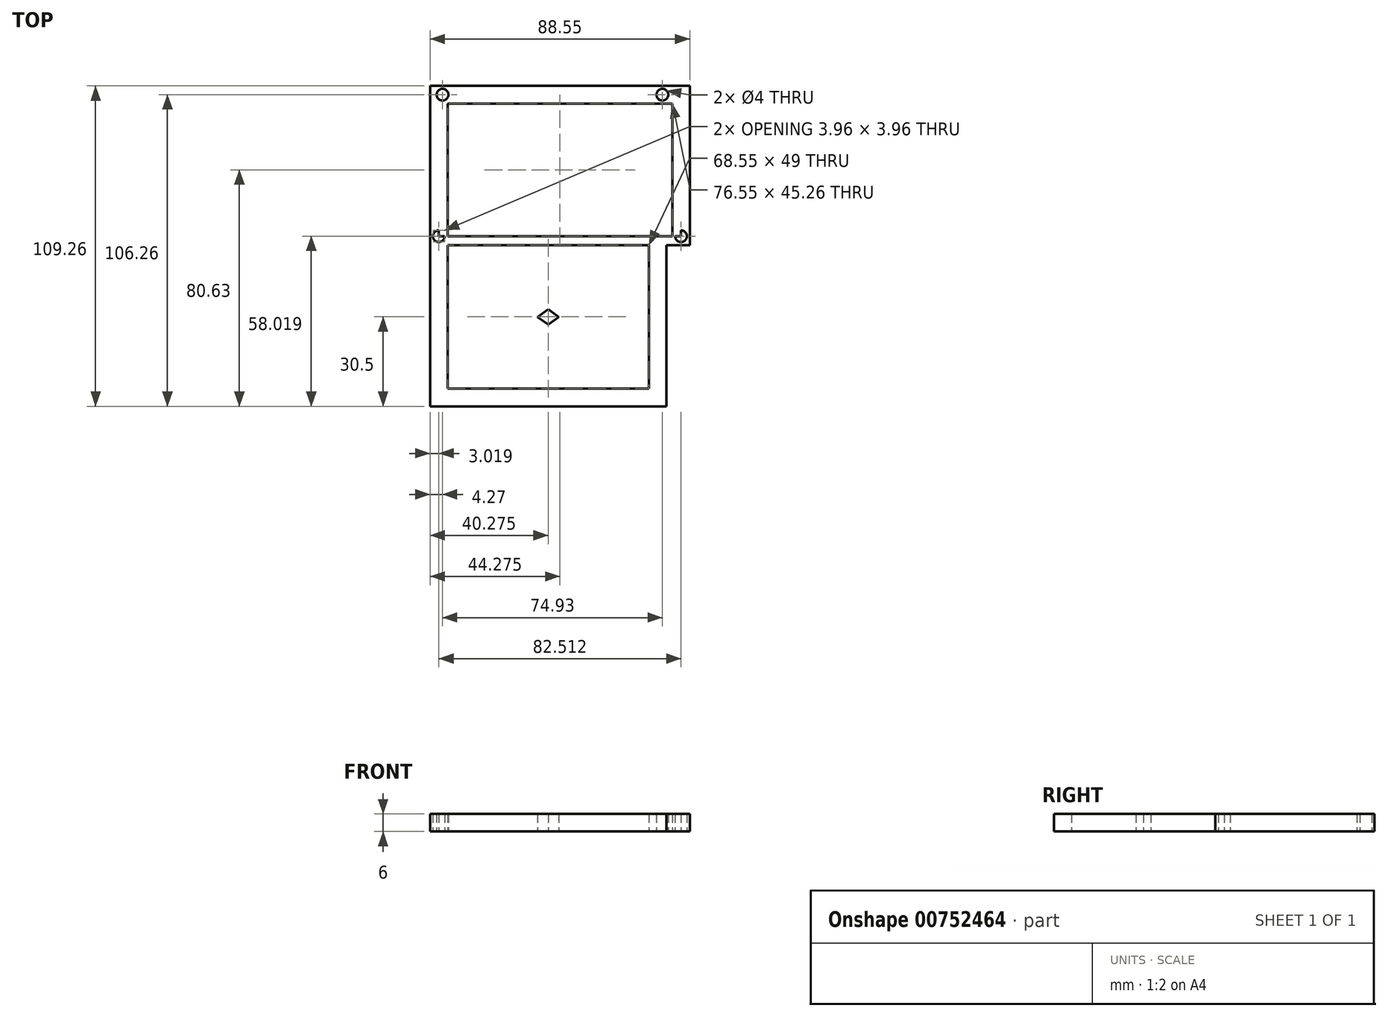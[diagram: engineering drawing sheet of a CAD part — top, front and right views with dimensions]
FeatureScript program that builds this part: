
annotation { "Feature Type Name" : "Feature", "Feature Type Description" : "" }
export const myFeature = defineFeature(function(context is Context, id is Id, definition is map)
    precondition{}
    {
        {
            var Q0;
            Q0=qCreatedBy(makeId("Top.planeOp"),FACE);
            var sketch = newSketch(context, id + "F0", { "sketchPlane" : qUnion([Q0])});
            skLineSegment(sketch, "E0", {"start": v(0, 0) * mm, "end": v(82.55, 0) * mm});
            skLineSegment(sketch, "E1", {"start": v(0, 0) * mm, "end": v(0, 48.26) * mm});
            skLineSegment(sketch, "E2", {"start": v(0, 48.26) * mm, "end": v(1.27, 48.26) * mm});
            skLineSegment(sketch, "E3", {"start": v(1.27, 48.26) * mm, "end": v(76.2, 48.26) * mm});
            skLineSegment(sketch, "E4", {"start": v(82.55, 0) * mm, "end": v(85.55, 0) * mm});
            skLineSegment(sketch, "E5", {"start": v(82.55, 0) * mm, "end": v(82.55, -3) * mm});
            skLineSegment(sketch, "E6", {"start": v(0, 0) * mm, "end": v(0, -3) * mm});
            skLineSegment(sketch, "E7", {"start": v(0, 0) * mm, "end": v(-3, 0) * mm});
            skLineSegment(sketch, "E8", {"start": v(0, 48.26) * mm, "end": v(-3, 48.26) * mm});
            skLineSegment(sketch, "E9", {"start": v(0, 48.26) * mm, "end": v(0, 51.26) * mm});
            skLineSegment(sketch, "E10", {"start": v(0, 51.26) * mm, "end": v(-3, 51.26) * mm});
            skLineSegment(sketch, "E11", {"start": v(-3, 51.26) * mm, "end": v(-3, 48.26) * mm});
            skLineSegment(sketch, "E12", {"start": v(0, -3) * mm, "end": v(-3, -3) * mm});
            skLineSegment(sketch, "E13", {"start": v(-3, 0) * mm, "end": v(-3, 48.26) * mm});
            skLineSegment(sketch, "E14", {"start": v(-3, 0) * mm, "end": v(-3, -3) * mm});
            skLineSegment(sketch, "E15", {"start": v(83.3, -3) * mm, "end": v(0, -3) * mm});
            skLineSegment(sketch, "E16", {"start": v(82.55, -3) * mm, "end": v(85.55, -3) * mm});
            skLineSegment(sketch, "E17", {"start": v(85.55, -3) * mm, "end": v(85.55, 0) * mm});
            skLineSegment(sketch, "E18", {"start": v(85.55, 0) * mm, "end": v(85.55, 51.26) * mm});
            skLineSegment(sketch, "E19", {"start": v(85.55, 51.26) * mm, "end": v(0, 51.26) * mm});
            skLineSegment(sketch, "E20", {"start": v(82.55, 0) * mm, "end": v(82.55, 48.26) * mm});
            skLineSegment(sketch, "E21", {"start": v(82.55, 48.26) * mm, "end": v(76.2, 48.26) * mm});
            skLineSegment(sketch, "E22", {"start": v(0, 48.26) * mm, "end": v(0, 45.26) * mm});
            skLineSegment(sketch, "E23", {"start": v(0, 45.26) * mm, "end": v(82.55, 45.26) * mm});
            skLineSegment(sketch, "E24", {"start": v(82.55, 0) * mm, "end": v(79.55, 0) * mm});
            skLineSegment(sketch, "E25", {"start": v(79.55, 0) * mm, "end": v(79.55, 45.26) * mm});
            skLineSegment(sketch, "E26", {"start": v(82.55, 0) * mm, "end": v(82.55, 3) * mm});
            skLineSegment(sketch, "E27", {"start": v(82.55, 3) * mm, "end": v(0, 3) * mm});
            skLineSegment(sketch, "E28", {"start": v(0, 0) * mm, "end": v(3, 0) * mm});
            skLineSegment(sketch, "E29", {"start": v(3, 0) * mm, "end": v(3, 45.26) * mm});
            skCircle(sketch, "E30", {"center": v(1.27, 48.26) * mm, "radius": 2 * mm});
            skCircle(sketch, "E31", {"center": v(76.2, 48.26) * mm, "radius": 2 * mm});
            skCircle(sketch, "E32", {"center": v(0, 0) * mm, "radius": 2 * mm});
            skCircle(sketch, "E33", {"center": v(82.55, 0) * mm, "radius": 2 * mm});
            skLineSegment(sketch, "E34", {"start": v(-3, -3) * mm, "end": v(-3, -58) * mm});
            skLineSegment(sketch, "E35", {"start": v(85.55, -3) * mm, "end": v(77.55, -3) * mm});
            skLineSegment(sketch, "E36", {"start": v(77.55, -3) * mm, "end": v(77.55, -58) * mm});
            skLineSegment(sketch, "E37", {"start": v(77.55, -58) * mm, "end": v(-3, -58) * mm});
            skLineSegment(sketch, "E38", {"start": v(-3, -58) * mm, "end": v(3, -58) * mm});
            skLineSegment(sketch, "E39", {"start": v(77.55, -58) * mm, "end": v(71.55, -58) * mm});
            skLineSegment(sketch, "E40", {"start": v(71.55, -58) * mm, "end": v(71.55, -3) * mm});
            skLineSegment(sketch, "E41", {"start": v(71.55, -58) * mm, "end": v(71.55, -52) * mm});
            skLineSegment(sketch, "E42", {"start": v(71.55, -52) * mm, "end": v(-3, -52) * mm});
            skLineSegment(sketch, "E43", {"start": v(3.07, -52) * mm, "end": v(6.07, -52) * mm});
            skLineSegment(sketch, "E44", {"start": v(3.07, -52) * mm, "end": v(3.07, -49) * mm});
            skLineSegment(sketch, "E45", {"start": v(71.55, -52) * mm, "end": v(71.55, -49) * mm});
            skLineSegment(sketch, "E46", {"start": v(71.55, -52) * mm, "end": v(68.55, -52) * mm});
            skLineSegment(sketch, "E47", {"start": v(71.55, -3) * mm, "end": v(71.55, -6) * mm});
            skLineSegment(sketch, "E48", {"start": v(71.55, -3) * mm, "end": v(68.55, -3) * mm});
            skLineSegment(sketch, "E49", {"start": v(3.07, -52) * mm, "end": v(3, -3) * mm});
            skLineSegment(sketch, "E50", {"start": v(3, -3) * mm, "end": v(6, -3) * mm});
            skLineSegment(sketch, "E51", {"start": v(3, -3) * mm, "end": v(3, -6) * mm});
            skLineSegment(sketch, "E52", {"start": v(3, -6) * mm, "end": v(68.55, -52) * mm});
            skLineSegment(sketch, "E53", {"start": v(71.55, -49) * mm, "end": v(6, -3) * mm});
            skLineSegment(sketch, "E54", {"start": v(68.55, -3) * mm, "end": v(3.07, -49) * mm});
            skLineSegment(sketch, "E55", {"start": v(71.55, -6) * mm, "end": v(6.07, -52) * mm});
            skSolve(sketch);
        }
        {
            var Q0;
            {var subQ1=sQuery(id+"F0.wireOp",EDGE,"E50");Q0=makeQuery(id+"F0.imprint","IMPRINT",FACE,{"disambiguationData":[TD([[makeQuery(id+"F0.imprint","IMPRINT",EDGE,{"derivedFrom":subQ1}),-1.0]])]});}
            var Q1;
            {var subQ0=sQuery(id+"F0.wireOp",EDGE,"E54");var subQ1=sQuery(id+"F0.wireOp",EDGE,"E52");var subQ2=makeQuery(id+"F0.imprint","INTERSECT",VERTEX,{"derivedFrom":[subQ1,subQ0]});Q1=makeQuery(id+"F0.imprint","IMPRINT",FACE,{"disambiguationData":[TD([[makeQuery(id+"F0.imprint","IMPRINT",EDGE,{"disambiguationData":[TD([[subQ2,-1.0]])],"derivedFrom":subQ1}),1.0]])]});}
            var Q2;
            {var subQ6=sQuery(id+"F0.wireOp",EDGE,"E47");Q2=makeQuery(id+"F0.imprint","IMPRINT",FACE,{"disambiguationData":[TD([[makeQuery(id+"F0.imprint","IMPRINT",EDGE,{"derivedFrom":subQ6}),-1.0]])]});}
            var Q3;
            {var subQ5=sQuery(id+"F0.wireOp",EDGE,"E45");Q3=makeQuery(id+"F0.imprint","IMPRINT",FACE,{"disambiguationData":[TD([[makeQuery(id+"F0.imprint","IMPRINT",EDGE,{"derivedFrom":subQ5}),1.0]])]});}
            var Q4;
            {var subQ6=sQuery(id+"F0.wireOp",EDGE,"E43");Q4=makeQuery(id+"F0.imprint","IMPRINT",FACE,{"disambiguationData":[TD([[makeQuery(id+"F0.imprint","IMPRINT",EDGE,{"derivedFrom":subQ6}),1.0]])]});}
            var Q5;
            {var subQ4=sQuery(id+"F0.wireOp",EDGE,"E12");Q5=makeQuery(id+"F0.imprint","IMPRINT",FACE,{"disambiguationData":[TD([[makeQuery(id+"F0.imprint","IMPRINT",EDGE,{"derivedFrom":subQ4}),1.0]])]});}
            var Q6;
            {var subQ10=sQuery(id+"F0.wireOp",EDGE,"E0");Q6=makeQuery(id+"F0.imprint","IMPRINT",FACE,{"disambiguationData":[TD([[makeQuery(id+"F0.imprint","IMPRINT",EDGE,{"derivedFrom":subQ10}),-1.0]])]});}
            var Q7;
            {var subQ1=sQuery(id+"F0.wireOp",EDGE,"E12");Q7=makeQuery(id+"F0.imprint","IMPRINT",FACE,{"disambiguationData":[TD([[makeQuery(id+"F0.imprint","IMPRINT",EDGE,{"derivedFrom":subQ1}),-1.0]])]});}
            var Q8;
            Q8=makeQuery(id+"F0.imprint","IMPRINT",FACE,{"disambiguationData":[TD([[makeQuery(id+"F0.imprint","IMPRINT",EDGE,{"derivedFrom":sQuery(id+"F0.wireOp",EDGE,"E37")}),-1.0]])]});
            var Q9;
            {var subQ0=sQuery(id+"F0.wireOp",EDGE,"E36");Q9=makeQuery(id+"F0.imprint","IMPRINT",FACE,{"disambiguationData":[TD([[makeQuery(id+"F0.imprint","IMPRINT",EDGE,{"derivedFrom":subQ0}),-1.0]])]});}
            var Q10;
            {var subQ10=sQuery(id+"F0.wireOp",EDGE,"E18");Q10=makeQuery(id+"F0.imprint","IMPRINT",FACE,{"disambiguationData":[TD([[makeQuery(id+"F0.imprint","IMPRINT",EDGE,{"derivedFrom":subQ10}),1.0]])]});}
            var Q11;
            {var subQ0=sQuery(id+"F0.wireOp",EDGE,"E17");Q11=makeQuery(id+"F0.imprint","IMPRINT",FACE,{"disambiguationData":[TD([[makeQuery(id+"F0.imprint","IMPRINT",EDGE,{"derivedFrom":subQ0}),1.0]])]});}
            var Q12;
            {var subQ3=sQuery(id+"F0.wireOp",EDGE,"E33");var subQ6=sQuery(id+"F0.wireOp",EDGE,"E24");var subQ9=makeQuery(id+"F0.imprint","INTERSECT",VERTEX,{"derivedFrom":[subQ6,subQ3]});Q12=makeQuery(id+"F0.imprint","IMPRINT",FACE,{"disambiguationData":[TD([[makeQuery(id+"F0.imprint","IMPRINT",EDGE,{"disambiguationData":[TD([[subQ9,1.0]])],"derivedFrom":subQ3}),-1.0]])]});}
            var Q13;
            {var subQ0=sQuery(id+"F0.wireOp",EDGE,"E0");Q13=makeQuery(id+"F0.imprint","IMPRINT",FACE,{"disambiguationData":[TD([[makeQuery(id+"F0.imprint","IMPRINT",EDGE,{"derivedFrom":subQ0}),1.0]])]});}
            var Q14;
            {var subQ1=sQuery(id+"F0.wireOp",EDGE,"E20");var subQ3=sQuery(id+"F0.wireOp",EDGE,"E23");var subQ4=makeQuery(id+"F0.imprint","INTERSECT",VERTEX,{"derivedFrom":[subQ1,subQ3]});Q14=makeQuery(id+"F0.imprint","IMPRINT",FACE,{"disambiguationData":[TD([[makeQuery(id+"F0.imprint","IMPRINT",EDGE,{"disambiguationData":[TD([[subQ4,1.0]])],"derivedFrom":subQ3}),-1.0]])]});}
            var Q15;
            {var subQ9=sQuery(id+"F0.wireOp",EDGE,"E30");var subQ11=sQuery(id+"F0.wireOp",EDGE,"E3");var subQ13=makeQuery(id+"F0.imprint","INTERSECT",VERTEX,{"derivedFrom":[subQ11,subQ9]});Q15=makeQuery(id+"F0.imprint","IMPRINT",FACE,{"disambiguationData":[TD([[makeQuery(id+"F0.imprint","IMPRINT",EDGE,{"disambiguationData":[TD([[subQ13,-1.0]])],"derivedFrom":subQ11}),-1.0]])]});}
            var Q16;
            {var subQ1=sQuery(id+"F0.wireOp",EDGE,"E1");var subQ3=sQuery(id+"F0.wireOp",EDGE,"E27");var subQ4=makeQuery(id+"F0.imprint","INTERSECT",VERTEX,{"derivedFrom":[subQ1,subQ3]});Q16=makeQuery(id+"F0.imprint","IMPRINT",FACE,{"disambiguationData":[TD([[makeQuery(id+"F0.imprint","IMPRINT",EDGE,{"disambiguationData":[TD([[subQ4,1.0]])],"derivedFrom":subQ3}),-1.0]])]});}
            var Q17;
            {var subQ0=sQuery(id+"F0.wireOp",EDGE,"E13");Q17=makeQuery(id+"F0.imprint","IMPRINT",FACE,{"disambiguationData":[TD([[makeQuery(id+"F0.imprint","IMPRINT",EDGE,{"derivedFrom":subQ0}),-1.0]])]});}
            var Q18;
            {var subQ3=sQuery(id+"F0.wireOp",EDGE,"E27");var subQ7=sQuery(id+"F0.wireOp",EDGE,"E1");var subQ8=makeQuery(id+"F0.imprint","INTERSECT",VERTEX,{"derivedFrom":[subQ7,subQ3]});Q18=makeQuery(id+"F0.imprint","IMPRINT",FACE,{"disambiguationData":[TD([[makeQuery(id+"F0.imprint","IMPRINT",EDGE,{"disambiguationData":[TD([[subQ8,1.0]])],"derivedFrom":subQ7}),-1.0]])]});}
            var Q19;
            {var subQ6=sQuery(id+"F0.wireOp",EDGE,"E10");Q19=makeQuery(id+"F0.imprint","IMPRINT",FACE,{"disambiguationData":[TD([[makeQuery(id+"F0.imprint","IMPRINT",EDGE,{"derivedFrom":subQ6}),1.0]])]});}
            extrude(context, id + "F1", {"entities" : qUnion([Q0, Q1, Q2, Q3, Q4, Q5, Q6, Q7, Q8, Q9, Q10, Q11, Q12, Q13, Q14, Q15, Q16, Q17, Q18, Q19]), "depth" : 6 * mm, "offsetDistance" : 25 * mm});
        }
    });
